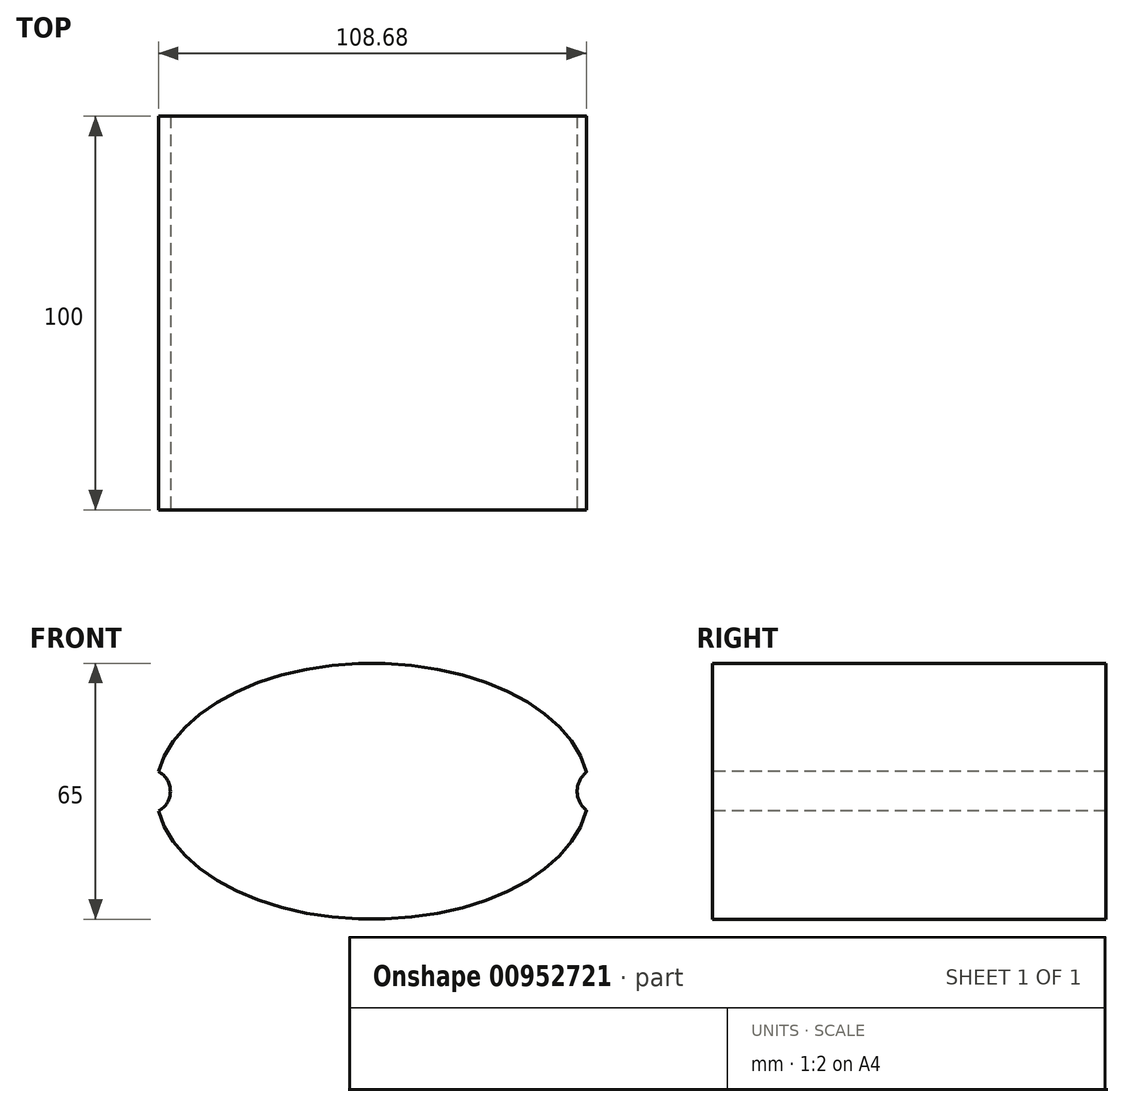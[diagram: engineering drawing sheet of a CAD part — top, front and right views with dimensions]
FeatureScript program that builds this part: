
annotation { "Feature Type Name" : "Feature", "Feature Type Description" : "" }
export const myFeature = defineFeature(function(context is Context, id is Id, definition is map)
    precondition{}
    {
        {
            var Q0;
            Q0=qCreatedBy(makeId("Front.planeOp"),FACE);
            var sketch = newSketch(context, id + "F0", { "sketchPlane" : qUnion([Q0])});
            skEllipticalArc(sketch, "E0", {});
            skArc(sketch, "E1", {"start": v(54.15, 4.62) * mm, "mid": v(52, 0) * mm, "end": v(54.15, -4.62) * mm});
            skPoint(sketch, "E2", {"position": v(52, 0) * mm});
            skPoint(sketch, "E3", {"position": v(55, 0) * mm});
            skArc(sketch, "E4.MirrorCS", {"start": v(-54.35, 5) * mm, "mid": v(-51.35, 0) * mm, "end": v(-54.35, -5) * mm});
            skEllipticalArc(sketch, "E5.trimOffspring", {});
            skPoint(sketch, "E6", {"position": v(0, 32.5) * mm});
            skEllipticalArc(sketch, "E7", {"construction": true});
            skEllipticalArc(sketch, "E8.trimOffspring", {"construction": true});
            skPoint(sketch, "E9", {"position": v(-51.35, 0) * mm});
            skPoint(sketch, "E10", {"position": v(-55, 0) * mm});
            skArc(sketch, "E11.filletArc", {"start": v(54.15, 4.62) * mm, "mid": v(54.3, 4.85) * mm, "end": v(54.31, 5.13) * mm});
            skPoint(sketch, "E12.visualSharp", {"position": v(54.4, -4.81) * mm});
            skArc(sketch, "E12.filletArc", {"start": v(54.31, -5.13) * mm, "mid": v(54.3, -4.85) * mm, "end": v(54.15, -4.62) * mm});
            skPoint(sketch, "E13", {"position": v(54.33, 5) * mm});
            const initialGuessF0  = {"E0": [0, 0, 1, 0, 0.055, 0.0325, 0.15852711916885184, 2.9871330551056094], "E5.trimOffspring": [0, 0, 1, 0, 0.055, 0.0325, 3.296052252073975, 6.124658188010733], "E7": [0, 0, 1, 0, 0.055, 0.0325, 2.9871330551056094, 3.296052252073976], "E8.trimOffspring": [0, 0, 1, 0, 0.055, 0.0325, 6.134570488568665, 0.148614818610921]};
            skSetInitialGuess(sketch, initialGuessF0);
            skSolve(sketch);
        }
        {
            var Q0;
            Q0 = qSketchRegion(id + "F0", true);
            extrude(context, id + "F1", {"entities" : qUnion([Q0]), "oppositeDirection" : true, "depth" : 100 * mm, "offsetDistance" : 25 * mm});
        }
    });
